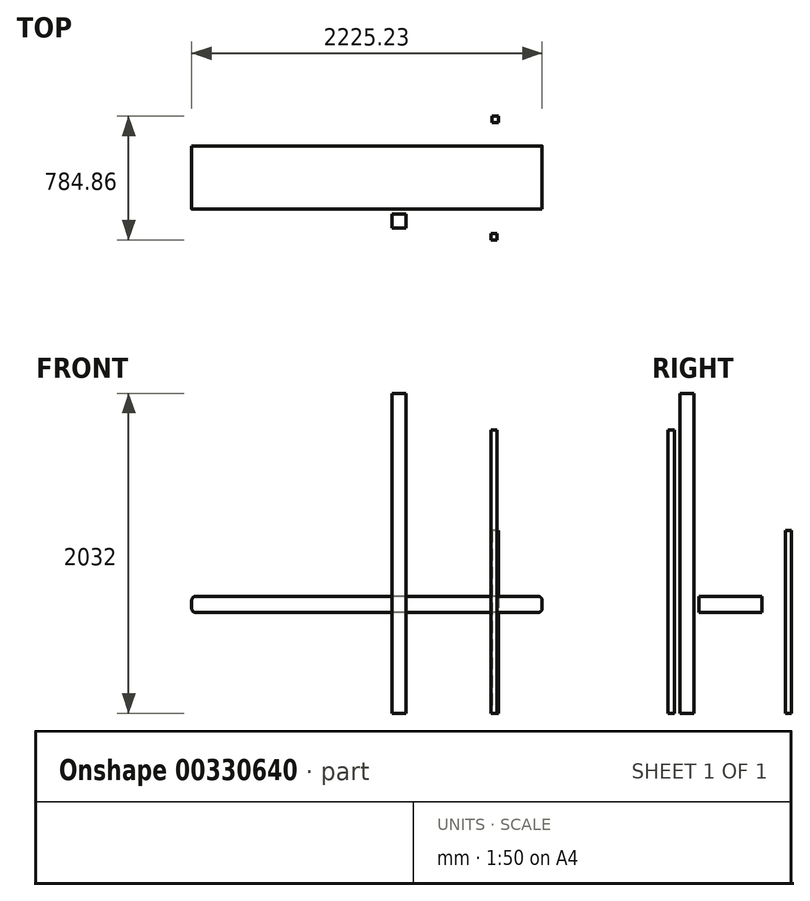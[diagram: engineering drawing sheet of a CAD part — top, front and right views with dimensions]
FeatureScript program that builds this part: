
annotation { "Feature Type Name" : "Feature", "Feature Type Description" : "" }
export const myFeature = defineFeature(function(context is Context, id is Id, definition is map)
    precondition{}
    {
        {
            var Q0;
            Q0=qCreatedBy(makeId("Top.planeOp"),FACE);
            var sketch = newSketch(context, id + "F0", { "sketchPlane" : qUnion([Q0])});
            skLineSegment(sketch, "E0.bottom", {"start": v(-1031.26, 470.92) * mm, "end": v(579.99, 470.92) * mm});
            skLineSegment(sketch, "E0.top", {"start": v(-1031.26, -799.08) * mm, "end": v(579.99, -799.08) * mm});
            skLineSegment(sketch, "E0.left", {"start": v(-1031.26, 470.92) * mm, "end": v(-1031.26, -799.08) * mm});
            skLineSegment(sketch, "E0.right", {"start": v(579.99, 470.92) * mm, "end": v(579.99, -799.08) * mm});
            skLineSegment(sketch, "E1.bottom", {"start": v(-811.3, -430.78) * mm, "end": v(-722.4, -430.78) * mm});
            skLineSegment(sketch, "E1.top", {"start": v(-811.3, -519.68) * mm, "end": v(-722.4, -519.68) * mm});
            skLineSegment(sketch, "E1.left", {"start": v(-811.3, -430.78) * mm, "end": v(-811.3, -519.68) * mm});
            skLineSegment(sketch, "E1.right", {"start": v(-722.4, -430.78) * mm, "end": v(-722.4, -519.68) * mm});
            skLineSegment(sketch, "E2.left", {"start": v(-1695.23, -203.79) * mm, "end": v(-1695.23, -124.38) * mm});
            skLineSegment(sketch, "E3.right", {"start": v(-1579.78, -371.2) * mm, "end": v(-1579.78, 9.8) * mm});
            skLineSegment(sketch, "E4.bottom", {"start": v(-135.13, 149.26) * mm, "end": v(-175, 149.26) * mm});
            skLineSegment(sketch, "E4.top", {"start": v(-135.13, 189.14) * mm, "end": v(-175, 189.14) * mm});
            skLineSegment(sketch, "E4.left", {"start": v(-135.13, 149.26) * mm, "end": v(-135.13, 189.14) * mm});
            skLineSegment(sketch, "E4.right", {"start": v(-175, 149.26) * mm, "end": v(-175, 189.14) * mm});
            skLineSegment(sketch, "E5.bottom", {"start": v(-183.66, -595.72) * mm, "end": v(-143.78, -595.72) * mm});
            skLineSegment(sketch, "E5.top", {"start": v(-183.66, -555.84) * mm, "end": v(-143.78, -555.84) * mm});
            skLineSegment(sketch, "E5.left", {"start": v(-183.66, -595.72) * mm, "end": v(-183.66, -555.84) * mm});
            skLineSegment(sketch, "E5.right", {"start": v(-143.78, -595.72) * mm, "end": v(-143.78, -555.84) * mm});
            skSolve(sketch);
        }
        {
            var Q0;
            Q0=makeQuery(id+"F0.imprint","IMPRINT",FACE,{"disambiguationData":[TD([[makeQuery(id+"F0.imprint","IMPRINT",EDGE,{"derivedFrom":sQuery(id+"F0.wireOp",EDGE,"E1.bottom")}),-1.0]])]});
            extrude(context, id + "F1", {"entities" : qUnion([Q0]), "depth" : 2032 * mm});
        }
        {
            var Q0;
            Q0=qCreatedBy(makeId("Front.planeOp"),FACE);
            var sketch = newSketch(context, id + "F2", { "sketchPlane" : qUnion([Q0])});
            skLineSegment(sketch, "E6.bottom", {"start": v(141.99, 639.83) * mm, "end": v(-2083.24, 639.83) * mm});
            skLineSegment(sketch, "E6.top", {"start": v(141.99, 742.33) * mm, "end": v(-2083.24, 742.33) * mm});
            skLineSegment(sketch, "E6.left", {"start": v(141.99, 639.83) * mm, "end": v(141.99, 742.33) * mm});
            skLineSegment(sketch, "E6.right", {"start": v(-2083.24, 639.83) * mm, "end": v(-2083.24, 742.33) * mm});
            skSolve(sketch);
        }
        {
            var Q0;
            Q0 = qSketchRegion(id + "F2", true);
            extrude(context, id + "F3", {"entities" : qUnion([Q0]), "depth" : 400.8 * mm});
        }
        {
            var Q0;
            Q0=makeQuery(id+"F3.opExtrude","SWEPT_EDGE",EDGE,{"disambiguationData":[OSD([sQuery(id+"F2.wireOp",EDGE,"E6.top"),sQuery(id+"F2.wireOp",EDGE,"E6.right")])]});
            var Q1;
            Q1=makeQuery(id+"F3.opExtrude","SWEPT_EDGE",EDGE,{"disambiguationData":[OSD([sQuery(id+"F2.wireOp",EDGE,"E6.top"),sQuery(id+"F2.wireOp",EDGE,"E6.left")])]});
            var Q2;
            Q2=makeQuery(id+"F3.opExtrude","SWEPT_EDGE",EDGE,{"disambiguationData":[OSD([sQuery(id+"F2.wireOp",EDGE,"E6.bottom"),sQuery(id+"F2.wireOp",EDGE,"E6.right")])]});
            var Q3;
            Q3=makeQuery(id+"F3.opExtrude","SWEPT_EDGE",EDGE,{"disambiguationData":[OSD([sQuery(id+"F2.wireOp",EDGE,"E6.bottom"),sQuery(id+"F2.wireOp",EDGE,"E6.left")])]});
            fillet(context, id + "F4", {"entities" : qUnion([Q0, Q1, Q2, Q3]), "radius" : 25.4 * mm, "tangentPropagation" : true, "allowEdgeOverflow" : false});
        }
        {
            var Q0;
            Q0=makeQuery(id+"F0.imprint","IMPRINT",FACE,{"disambiguationData":[TD([[makeQuery(id+"F0.imprint","IMPRINT",EDGE,{"derivedFrom":sQuery(id+"F0.wireOp",EDGE,"E4.bottom")}),-1.0]])]});
            extrude(context, id + "F5", {"entities" : qUnion([Q0]), "depth" : 1160.02 * mm});
        }
        {
            var Q0;
            Q0=makeQuery(id+"F0.imprint","IMPRINT",FACE,{"disambiguationData":[TD([[makeQuery(id+"F0.imprint","IMPRINT",EDGE,{"derivedFrom":sQuery(id+"F0.wireOp",EDGE,"E5.bottom")}),1.0]])]});
            extrude(context, id + "F6", {"entities" : qUnion([Q0]), "depth" : 1799.84 * mm});
        }
    });
